# Revit family: Towel_Bar_Holder-Grohe-ATRIO-40309_Series
name_source: partatom
category: Specialty Equipment
units: mm (PartAtom-declared; Revit-internal decimal feet)

## family parameters
Cut with Voids When Loaded = No
Host = Face
OmniClass Number = 23.40.20.21.27
OmniClass Title = Towel Bars
Part Type = Normal
Room Calculation Point = No
Round Connector Dimension = Use Diameter
Shared = Yes

## types (2) — shared parameters
ASME A112.18.1/CSA B125.1 = Yes
Assembly Code = C1030200
Default Elevation = 1016 mm
Description = Atrio Towel Rail
Energy Policy Act of 1992 = Yes
Height = 35 mm  [stored 0.114829 ft]
Installation Instruction Link = https://americanstandard.box.com
Installation Type = Wall Mounted
Length = 66 mm
Manufacturer = Grohe
Price = Prices may vary. Please consult Manufacturer Representative for most up-to-date price list.
Product Documentation Link = https://americanstandard.box.com
Product Page URL = https://www.grohe.us
Revised Date = 11/01/2021
URL = https://www.grohe.us
Warranty Documentation Link = https://cdn.cloud.grohe.com
Width = 642 mm  [stored 2.1063 ft]

## per-type parameters (varying)
| type | Finish | Material |
| 40309003 | Metal-Grohe-003-Starlight Chrome | Metal-Grohe-003-Starlight Chrome |
| 40309EN3 | Metal-Grohe-EN3-Brushed Nickel Infinity Finish | Metal-Grohe-EN3-Brushed Nickel Infinity Finish |

note: column(s) folded — value = type name in every type: Model

note: [stored X ft] marks values corroborated as IEEE doubles in the binary element streams (Revit-internal decimal feet)

## geometry (parser evidence)
native form markers: Sweep x5
no freeform markers — native parametric forms only
